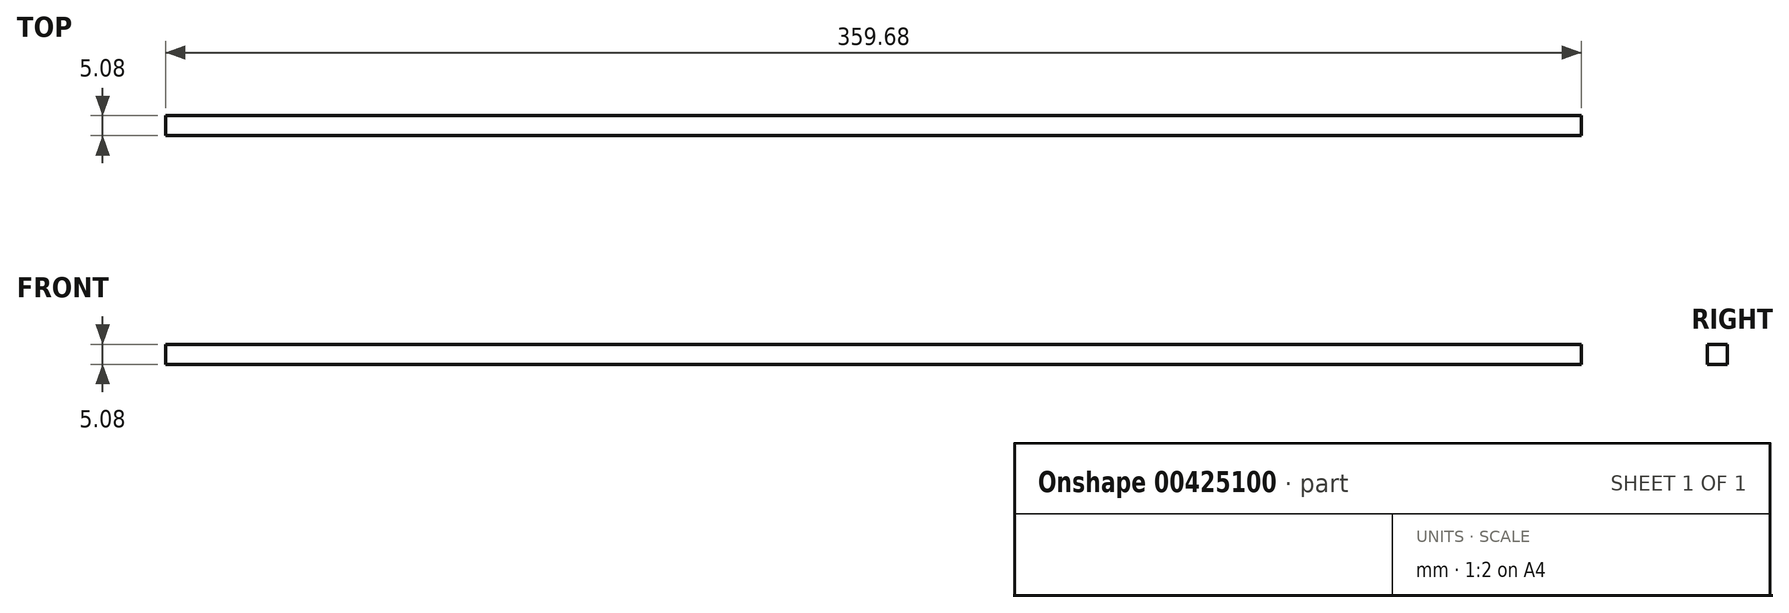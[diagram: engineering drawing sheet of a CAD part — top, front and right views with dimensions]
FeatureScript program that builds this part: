
annotation { "Feature Type Name" : "Feature", "Feature Type Description" : "" }
export const myFeature = defineFeature(function(context is Context, id is Id, definition is map)
    precondition{}
    {
        {
            var Q0;
            Q0=qCreatedBy(makeId("Front.planeOp"),FACE);
            var sketch = newSketch(context, id + "F0", { "sketchPlane" : qUnion([Q0])});
            skLineSegment(sketch, "E0.bottom", {"start": v(-156.46, -81.68) * mm, "end": v(203.22, -81.68) * mm});
            skLineSegment(sketch, "E0.top", {"start": v(-156.46, -86.76) * mm, "end": v(203.22, -86.76) * mm});
            skLineSegment(sketch, "E0.left", {"start": v(-156.46, -81.68) * mm, "end": v(-156.46, -86.76) * mm});
            skLineSegment(sketch, "E0.right", {"start": v(203.22, -81.68) * mm, "end": v(203.22, -86.76) * mm});
            skSolve(sketch);
        }
        {
            var Q0;
            Q0 = qSketchRegion(id + "F0", true);
            extrude(context, id + "F1", {"entities" : qUnion([Q0]), "depth" : 5.08 * mm});
        }
    });
